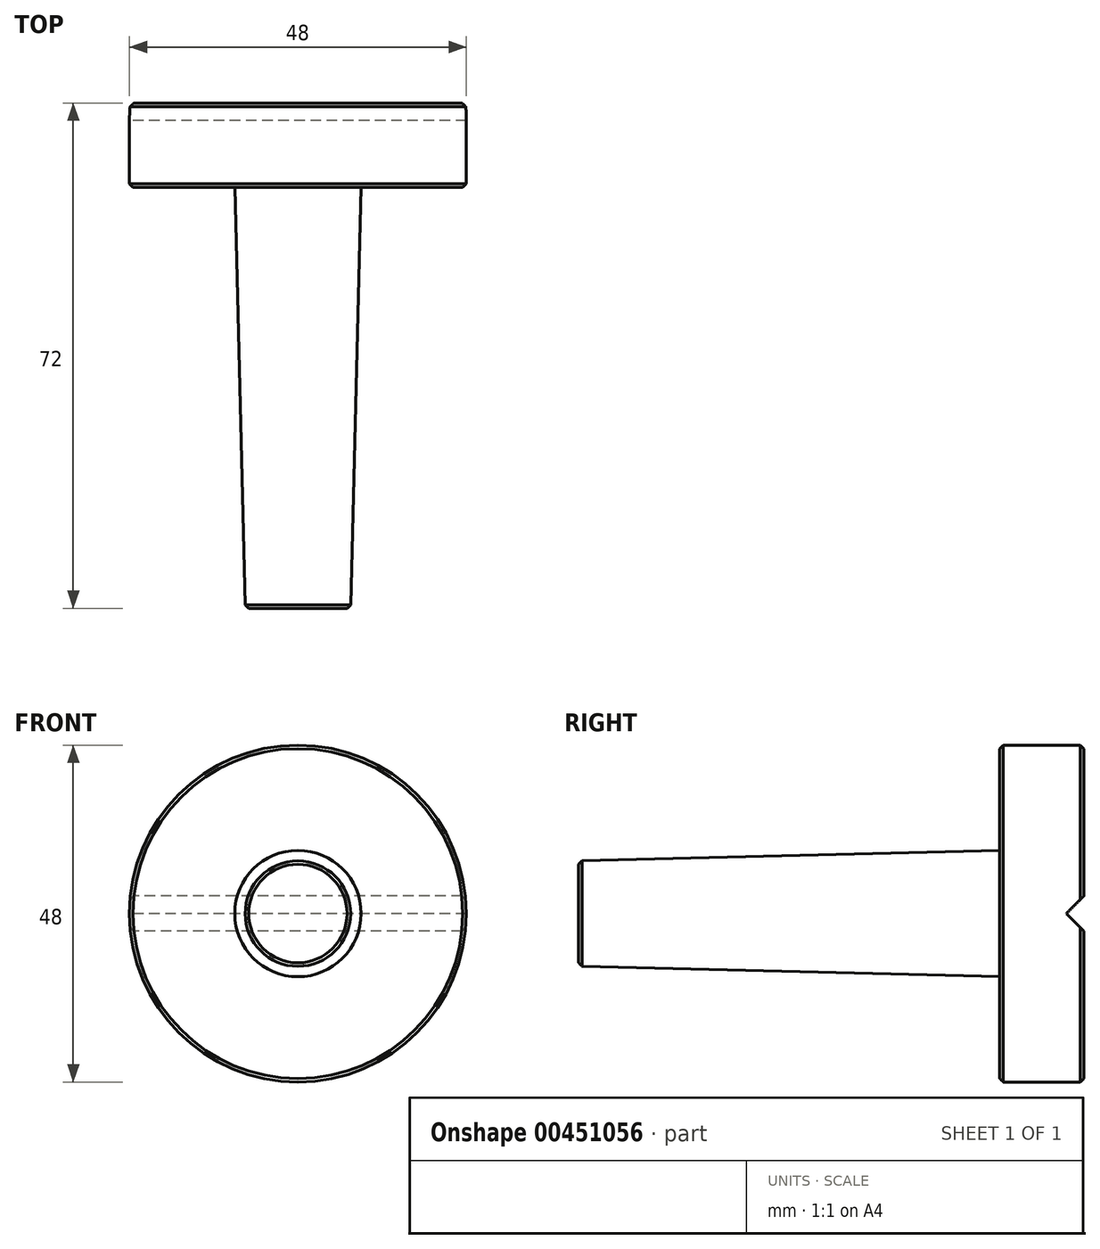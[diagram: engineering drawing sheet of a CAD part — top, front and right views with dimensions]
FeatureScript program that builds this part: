
annotation { "Feature Type Name" : "Feature", "Feature Type Description" : "" }
export const myFeature = defineFeature(function(context is Context, id is Id, definition is map)
    precondition{}
    {
        {
            var Q0;
            Q0=qCreatedBy(makeId("Right.planeOp"),FACE);
            var sketch = newSketch(context, id + "F0", { "sketchPlane" : qUnion([Q0])});
            skLineSegment(sketch, "E0", {"start": v(0, 9) * mm, "end": v(0, 24) * mm});
            skLineSegment(sketch, "E1", {"start": v(0, 24) * mm, "end": v(12, 24) * mm});
            skLineSegment(sketch, "E2", {"start": v(12, 24) * mm, "end": v(12, 0) * mm});
            skLineSegment(sketch, "E3", {"start": v(12, 0) * mm, "end": v(-60, 0) * mm});
            skLineSegment(sketch, "E4", {"start": v(-60, 0) * mm, "end": v(-60, 7.5) * mm});
            skLineSegment(sketch, "E5", {"start": v(-60, 7.5) * mm, "end": v(0, 9) * mm});
            skLineSegment(sketch, "E6", {"start": v(0, 0) * mm, "end": v(61.68, 0) * mm, "construction": true});
            skSolve(sketch);
        }
        {
            var Q0;
            Q0 = qSketchRegion(id + "F0", true);
            var Q1;
            Q1=sQuery(id+"F0.wireOp",EDGE,"E6");
            revolve(context, id + "F1", {"entities" : qUnion([Q0]), "axis" : qUnion([Q1]), "revolveType" : RevolveType.FULL});
        }
        {
            var Q0;
            Q0=qCreatedBy(makeId("Right.planeOp"),FACE);
            var sketch = newSketch(context, id + "F2", { "sketchPlane" : qUnion([Q0])});
            skLineSegment(sketch, "E7", {"start": v(12, 2.5) * mm, "end": v(9.5, 0) * mm});
            skLineSegment(sketch, "E8", {"start": v(9.5, 0) * mm, "end": v(12, -2.5) * mm});
            skLineSegment(sketch, "E9.0", {"start": v(12, -2.5) * mm, "end": v(12, 2.5) * mm});
            skPoint(sketch, "E10.orphan", {"position": v(12, 24) * mm});
            skPoint(sketch, "E11.orphan", {"position": v(12, -24) * mm});
            skSolve(sketch);
        }
        {
            var Q0;
            Q0 = qSketchRegion(id + "F2", true);
            extrude(context, id + "F3", {"entities" : qUnion([Q0]), "operationType" : NewBodyOperationType.REMOVE, "endBound" : BoundingType.THROUGH_ALL, "depth" : 25 * mm, "hasSecondDirection" : true, "secondDirectionBound" : SecondDirectionBoundingType.THROUGH_ALL, "secondDirectionOppositeDirection" : true, "secondDirectionDepth" : 25 * mm});
        }
        {
            var Q0;
            Q0=makeQuery(id+"F1.opRevolve","SWEPT_EDGE",EDGE,{"disambiguationData":[OSD([sQuery(id+"F0.wireOp",EDGE,"E4"),sQuery(id+"F0.wireOp",EDGE,"E5")])]});
            var Q1;
            Q1=makeQuery(id+"F1.opRevolve","SWEPT_EDGE",EDGE,{"disambiguationData":[OSD([sQuery(id+"F0.wireOp",EDGE,"E0"),sQuery(id+"F0.wireOp",EDGE,"E1")])]});
            var Q2;
            {var subQ0=sQuery(id+"F0.wireOp",EDGE,"E1");var subQ1=sQuery(id+"F0.wireOp",EDGE,"E2");Q2=makeQuery(id+"F3.boolean.opBoolean","SPLIT",EDGE,{"disambiguationData":[TD([makeQuery(id+"F3.opExtrude","SWEPT_FACE",FACE,{"disambiguationData":[OSD([sQuery(id+"F2.wireOp",EDGE,"E7")])]})])],"derivedFrom":makeQuery(id+"F1.opRevolve","SWEPT_EDGE",EDGE,{"disambiguationData":[OSD([subQ0,subQ1])]})});}
            var Q3;
            {var subQ0=sQuery(id+"F0.wireOp",EDGE,"E1");var subQ1=sQuery(id+"F0.wireOp",EDGE,"E2");Q3=makeQuery(id+"F3.boolean.opBoolean","SPLIT",EDGE,{"disambiguationData":[TD([makeQuery(id+"F3.opExtrude","SWEPT_FACE",FACE,{"disambiguationData":[OSD([sQuery(id+"F2.wireOp",EDGE,"E8")])]})])],"derivedFrom":makeQuery(id+"F1.opRevolve","SWEPT_EDGE",EDGE,{"disambiguationData":[OSD([subQ0,subQ1])]})});}
            chamfer(context, id + "F4", {"entities" : qUnion([Q0, Q1, Q2, Q3]), "width" : .5 * mm, "tangentPropagation" : true});
        }
    });
